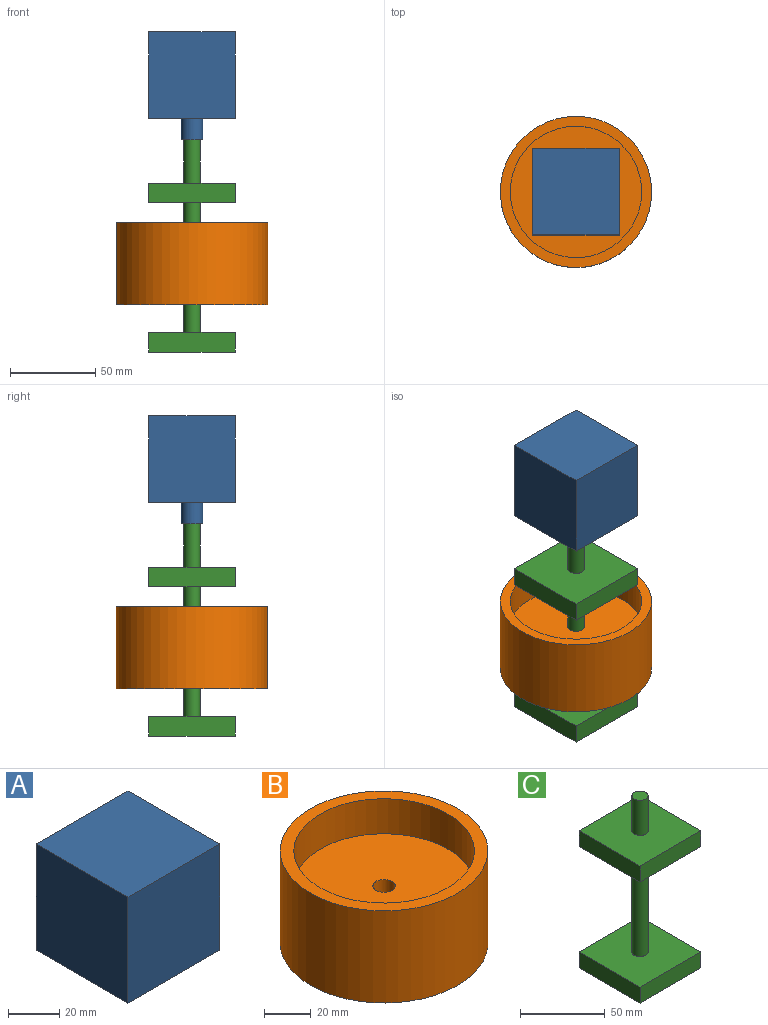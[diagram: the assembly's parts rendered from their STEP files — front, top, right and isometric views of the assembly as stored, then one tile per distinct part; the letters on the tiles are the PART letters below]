
ASSEMBLY  parts=3 mates=4
PART A: 10 faces, bbox 50.8x63.5x50.8 mm
  f0: plane 50.8x50.8mm, normal (0,0,-1), area 2580.6mm2, adj f1,f3,f4,f5
  f1: plane 50.8x50.8mm, normal (1,0,0), area 2580.6mm2, adj f0,f2,f4,f5
  f2: plane 50.8x50.8mm, normal (0,0,1), area 2580.6mm2, adj f1,f3,f4,f5
  f3: plane 50.8x50.8mm, normal (-1,0,0), area 2580.6mm2, adj f0,f2,f4,f5
  f4: plane 50.8x50.8mm, normal (0,-1,0), area 2580.6mm2, adj f0,f1,f2,f3
  f5: plane 50.8x50.8mm, normal (0,1,0), area 2454mm2, adj f0,f1,f2,f3,f7
  f6: cylinder r=1.27mm len=12.7mm, axis (0,-1,0), area 101.3mm2, adj f8,f9
  f7: cylinder r=6.35mm len=12.7mm, axis (0,-1,0), area 506.7mm2, adj f5,f8
  f8: plane 12.7x12.7mm, normal (0,1,0), area 121.6mm2, adj f6,f7
  f9: plane 2.54x2.54mm, normal (0,1,0), area 5.1mm2, adj f6
PART B: 8 faces, bbox 88.9x88.9x48.3 mm
  f0: cylinder r=38.63mm len=77.27mm, axis (0,0,1), area 4451.6mm2, adj f4,f7
  f1: cylinder r=44.45mm len=88.9mm, axis (0,0,1), area 13478.4mm2, adj f2,f4
  f2: plane 88.9x88.9mm, normal (0,0,1), area 1518.2mm2, adj f1,f3
  f3: cylinder r=38.63mm len=77.27mm, axis (0,0,1), area 4451.6mm2, adj f2,f6
  f4: plane 88.9x88.9mm, normal (0,0,-1), area 1518.2mm2, adj f0,f1
  f5: cylinder r=4.76mm len=11.58mm, axis (0,0,-1), area 346.6mm2, adj f6,f7
  f6: plane 77.27x77.27mm, normal (0,0,1), area 4617.7mm2, adj f3,f5
  f7: plane 77.27x77.27mm, normal (0,0,-1), area 4617.7mm2, adj f0,f5
PART C: 15 faces, bbox 50.8x50.8x124.8 mm
  f0: plane 50.8x11.58mm, normal (0,-1,0), area 588.4mm2, adj f1,f3,f4,f5
  f1: plane 50.8x11.58mm, normal (1,0,0), area 588.4mm2, adj f0,f2,f4,f5
  f2: plane 50.8x11.58mm, normal (0,1,0), area 588.4mm2, adj f1,f3,f4,f5
  f3: plane 50.8x11.58mm, normal (-1,0,0), area 588.4mm2, adj f0,f2,f4,f5
  f4: plane 50.8x50.8mm, normal (0,0,1), area 2509.4mm2, adj f0,f1,f2,f3,f6
  f5: plane 50.8x50.8mm, normal (0,0,-1), area 2580.6mm2, adj f0,f1,f2,f3
  f6: cylinder r=4.76mm len=76.2mm, axis (0,0,-1), area 2280.2mm2, adj f4,f12
  f7: plane 50.8x11.58mm, normal (0,-1,0), area 588.4mm2, adj f8,f10,f11,f12
  f8: plane 50.8x11.58mm, normal (1,0,0), area 588.4mm2, adj f7,f9,f11,f12
  f9: plane 50.8x11.58mm, normal (0,1,0), area 588.4mm2, adj f8,f10,f11,f12
  f10: plane 50.8x11.58mm, normal (-1,0,0), area 588.4mm2, adj f7,f9,f11,f12
  f11: plane 50.8x50.8mm, normal (0,0,1), area 2509.4mm2, adj f7,f8,f9,f10,f13
  f12: plane 50.8x50.8mm, normal (0,0,-1), area 2509.4mm2, adj f6,f7,f8,f9,f10
  f13: cylinder r=4.76mm len=25.4mm, axis (0,0,-1), area 760.1mm2, adj f11,f14
  f14: plane 9.53x9.53mm, normal (0,0,1), area 71.3mm2, adj f13
PLACE A rot(axis=(-0.58,0.58,-0.58),120deg) t=(0,0,137.46)mm
PLACE B rot(axis=(0,0,-1),71.3deg) t=(0,0,51.87)mm
PLACE C at identity fixed
MATE planar A.f2 <-> C.f8  axis (1,0,0) through (25.4,0,162.86)mm
MATE cylindrical A.f6 <-> C.f6  axis (0,0,-1) through (0,0,124.76)mm
MATE cylindrical B.f0 <-> C.f6  axis (0,0,-1) through (0,0,51.87)mm
MATE planar A.f6 <-> C.f6  axis (0,0,-1) through (0,0,124.76)mm
